# Revit family: 220-35 _VERTICAL PANEL 3 SIDED FRAME_STACKED TO ONE SIDE
name_source: partatom
category: Generic Models
revit_build: Autodesk Revit 2018 (Build: 20190510_1515(x64)
units: mm (PartAtom-declared; Revit-internal decimal feet)

## family parameters
Always vertical = Yes
Can host rebar = No
Cut with Voids When Loaded = No
Part Type = Normal
Room Calculation Point = No
Round Connector Dimension = Use Diameter
Shared = No
Work Plane-Based = No

## types (1)
- 220-35 _VERTICAL PANEL 3 SIDED FRAME_STACKED TO ONE SIDE
    220-35-VERTICAL BLADE = <By Category>
    ANGLE = 0.00°
    ANGLE INPUT = 0.00°
    ANGLE LIMIT = 0.00°
    ARRAY = 8
    BLACK-STRIP = <By Category>
    END CAP = <By Category>
    FRAME = <By Category>
    HEIGHT = 2500 mm  [stored 8.2021 ft]
    HEIGHT INPUT = 2500 mm  [stored 8.2021 ft]
    M1 = 116 mm
    REMAINDER = 181 mm  [stored 0.593832 ft]
    SPACING = 205 mm  [stored 0.672572 ft]
    SPACING INPUT = 205 mm  [stored 0.672572 ft]
    STACKED INPUT = 116 mm
    WIDTH = 2000 mm  [stored 6.56168 ft]
    WIDTH INPUT = 1821 mm  [stored 5.97441 ft]

note: [stored X ft] marks values corroborated as IEEE doubles in the binary element streams (Revit-internal decimal feet)

## geometry (parser evidence)
native form markers: Sweep x16
no freeform markers — native parametric forms only
